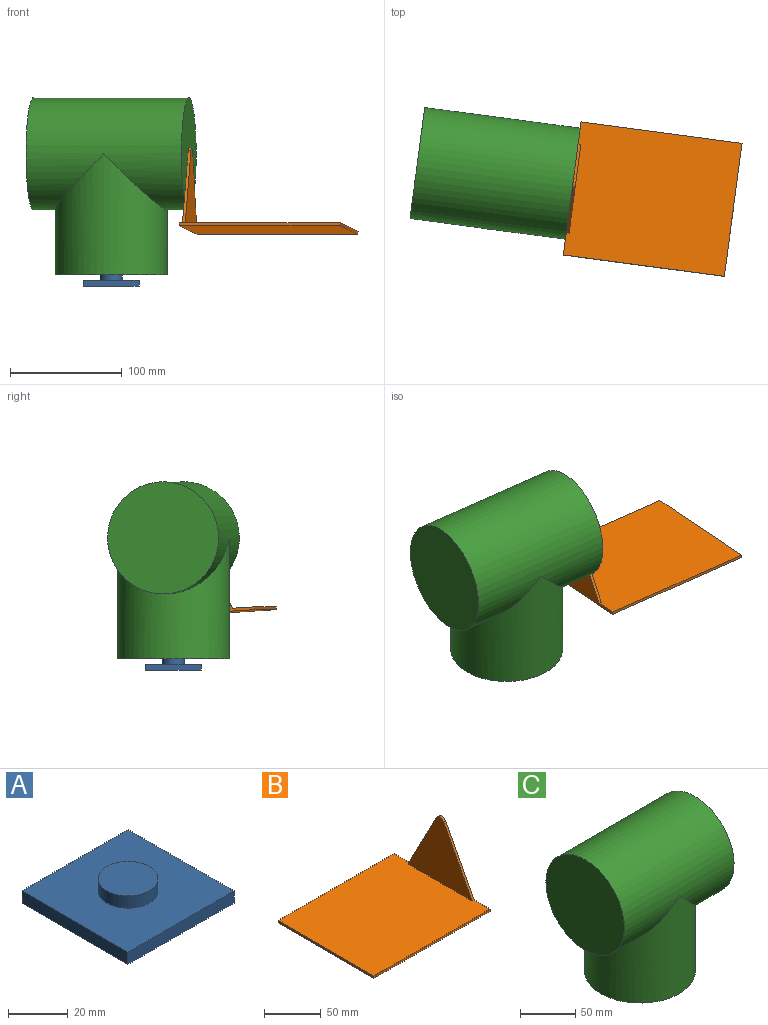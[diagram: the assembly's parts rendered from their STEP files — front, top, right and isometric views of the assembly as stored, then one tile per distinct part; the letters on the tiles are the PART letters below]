
ASSEMBLY  parts=3 mates=2
PART A: 8 faces, bbox 50x50x10 mm
  f0: plane 50x5mm, normal (0,-1,0), area 250mm2, adj f1,f3,f4,f5
  f1: plane 50x5mm, normal (1,0,0), area 250mm2, adj f0,f2,f4,f5
  f2: plane 50x5mm, normal (0,1,0), area 250mm2, adj f1,f3,f4,f5
  f3: plane 50x5mm, normal (-1,0,0), area 250mm2, adj f0,f2,f4,f5
  f4: plane 50x50mm, normal (0,0,1), area 2185.8mm2, adj f0,f1,f2,f3,f6
  f5: plane 50x50mm, normal (0,0,-1), area 2500mm2, adj f0,f1,f2,f3
  f6: cylinder r=10mm len=20mm, axis (0,0,-1), area 314.2mm2, adj f4,f7
  f7: plane 20x20mm, normal (0,0,1), area 314.2mm2, adj f6
PART B: 10 faces, bbox 145x120x73 mm
  f0: plane 145x2.5mm, normal (0,-1,0), area 362.5mm2, adj f1,f3,f4,f5
  f1: plane 120x73mm, normal (1,0,0), area 3330.1mm2, adj f0,f2,f4,f5,f6,f7,f8
  f2: plane 145x2.5mm, normal (0,1,0), area 362.5mm2, adj f1,f3,f4,f5
  f3: plane 120x2.5mm, normal (-1,0,0), area 300mm2, adj f0,f2,f4,f5
  f4: plane 145x120mm, normal (0,0,1), area 17200mm2, adj f0,f1,f2,f3,f6,f7,f9
  f5: plane 145x120mm, normal (0,0,-1), area 17400mm2, adj f0,f1,f2,f3
  f6: plane 67.82x35.57mm, normal (0,-0.89,0.46), area 191.5mm2, adj f1,f4,f8,f9
  f7: plane 67.82x35.57mm, normal (0,0.89,0.46), area 191.5mm2, adj f1,f4,f8,f9
  f8: cylinder r=5mm len=8.86mm, axis (1,0,0), area 27.2mm2, adj f1,f6,f7,f9
  f9: plane 80x70.5mm, normal (-1,0,0), area 3030.1mm2, adj f4,f6,f7,f8
PART C: 5 faces, bbox 140x100x158 mm
  f0: cylinder r=50mm len=108mm, axis (0,0,-1), area 23929.2mm2, adj f1,f2
  f1: plane 100x100mm, normal (0,0,-1), area 7854mm2, adj f0
  f2: cylinder r=50mm len=140mm, axis (-1,0,0), area 33982.3mm2, adj f0,f3,f4
  f3: plane 100x100mm, normal (1,0,0), area 7854mm2, adj f2
  f4: plane 100x100mm, normal (-1,0,0), area 7854mm2, adj f2
PLACE A t=(-0.07,0.01,-4.93)mm fixed
PLACE B rot(axis=(0,0.03,1),172.4deg) t=(140.63,-23.04,45.2)mm
PLACE C rot(axis=(0,0,-1),7.6deg) t=(-0.07,0.01,5.07)mm
MATE revolute C.f2 <-> B.f8  axis (0.99,-0.13,0) through (69.32,-9.22,113.07)mm
MATE revolute A.f6 <-> C.f0  axis (0,0,1) through (-0.07,0.01,5.07)mm
